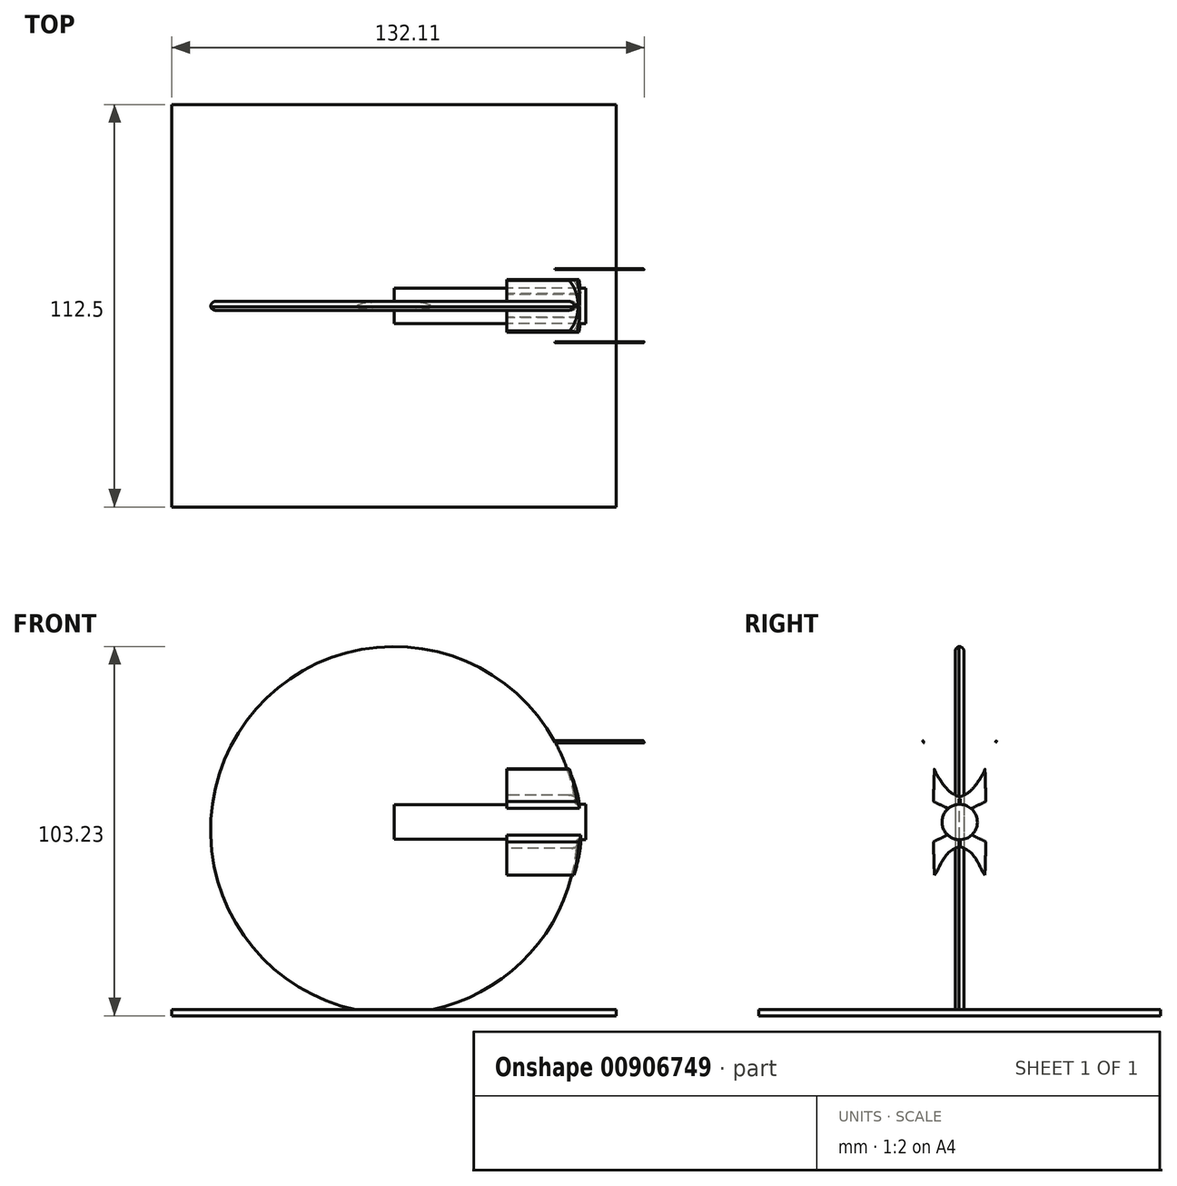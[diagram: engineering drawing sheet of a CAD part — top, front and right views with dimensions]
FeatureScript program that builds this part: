
annotation { "Feature Type Name" : "Feature", "Feature Type Description" : "" }
export const myFeature = defineFeature(function(context is Context, id is Id, definition is map)
    precondition{}
    {
        {
            var Q0;
            Q0=qCreatedBy(makeId("Top.planeOp"),FACE);
            var sketch = newSketch(context, id + "F0", { "sketchPlane" : qUnion([Q0])});
            skArc(sketch, "E0", {"start": v(0, -74.28) * mm, "mid": v(49.1, -56.16) * mm, "end": v(74.07, -10.16) * mm});
            skArc(sketch, "E1", {"start": v(74.12, 9.88) * mm, "mid": v(69.18, -0.13) * mm, "end": v(74.07, -10.16) * mm});
            skArc(sketch, "E2.trimOffspring", {"start": v(74.12, 9.88) * mm, "mid": v(49.23, 56.1) * mm, "end": v(0, 74.35) * mm});
            skLineSegment(sketch, "E3", {"start": v(0, 74.35) * mm, "end": v(0, -74.28) * mm});
            skArc(sketch, "E4", {"start": v(0, -72.43) * mm, "mid": v(75.07, 0.28) * mm, "end": v(0, 72.99) * mm});
            skSolve(sketch);
        }
        {
            var Q0;
            Q0=sQuery(id+"F0.wireOp",EDGE,"E4");
            var Q1;
            Q1=sQuery(id+"F0.wireOp",EDGE,"E3");
            revolve(context, id + "F1", {"bodyType" : ToolBodyType.SURFACE, "surfaceOperationType" : NewSurfaceOperationType.NEW, "surfaceEntities" : qUnion([Q0]), "axis" : qUnion([Q1]), "revolveType" : RevolveType.TWO_DIRECTIONS, "angle" : 10 * degree, "angleBack" : 355 * degree});
        }
        {
            var Q0;
            Q0=sQuery(id+"F0.wireOp",EDGE,"E1");
            var Q1;
            Q1=sQuery(id+"F0.wireOp",EDGE,"E2.trimOffspring");
            var Q2;
            Q2=sQuery(id+"F0.wireOp",EDGE,"E0");
            var Q3;
            Q3=sQuery(id+"F0.wireOp",EDGE,"E3");
            revolve(context, id + "F2", {"bodyType" : ToolBodyType.SURFACE, "surfaceOperationType" : NewSurfaceOperationType.NEW, "surfaceEntities" : qUnion([Q0, Q1, Q2]), "axis" : qUnion([Q3]), "revolveType" : RevolveType.FULL});
        }
        {
            var Q0;
            Q0=qCreatedBy(makeId("Right.planeOp"),FACE);
            cPlane(context, id + "F3", {"entities" : qUnion([Q0]), "cplaneType" : CPlaneType.OFFSET, "offset" : 75 * mm, "width" : 150 * mm, "height" : 150 * mm});
        }
        {
            var Q0;
            Q0=qCreatedBy(id+"F3.planeOp",FACE);
            var sketch = newSketch(context, id + "F4", { "sketchPlane" : qUnion([Q0])});
            skLineSegment(sketch, "E5", {"start": v(0.28, 7.52) * mm, "end": v(0.28, 12.5) * mm});
            skLineSegment(sketch, "E6.MirrorCS", {"start": v(-0.28, 7.52) * mm, "end": v(-0.28, 12.5) * mm});
            skLineSegment(sketch, "E7", {"start": v(0.28, -2.1) * mm, "end": v(0.28, -6.23) * mm});
            skLineSegment(sketch, "E8", {"start": v(-0.28, -2.1) * mm, "end": v(-0.28, -6.23) * mm});
            skCircle(sketch, "E9", {"center": v(0, 3.4) * mm, "radius": 4.14 * mm});
            skLineSegment(sketch, "E10", {"start": v(-0.28, -2.1) * mm, "end": v(-0.28, -0.73) * mm});
            skLineSegment(sketch, "E11", {"start": v(-0.28, -0.73) * mm, "end": v(0.28, -0.73) * mm});
            skLineSegment(sketch, "E12", {"start": v(0.28, -0.73) * mm, "end": v(0.28, -2.1) * mm});
            skPoint(sketch, "E13.orphan", {"position": v(-0.28, 7.2) * mm});
            skPoint(sketch, "E14.orphan", {"position": v(0.28, 7.2) * mm});
            skLineSegment(sketch, "E15", {"start": v(0.28, -6.23) * mm, "end": v(0.28, -6.53) * mm});
            skLineSegment(sketch, "E16", {"start": v(-0.28, -6.23) * mm, "end": v(-0.28, -6.54) * mm});
            skPoint(sketch, "E17.end.orphan", {"position": v(0.28, 13.7) * mm});
            skPoint(sketch, "E17.start.orphan", {"position": v(-0.28, 13.7) * mm});
            skLineSegment(sketch, "E18", {"start": v(-0.28, 12.5) * mm, "end": v(0.28, 12.5) * mm});
            skLineSegment(sketch, "E19", {"start": v(0.28, -6.53) * mm, "end": v(0.28, -6.67) * mm});
            skLineSegment(sketch, "E20", {"start": v(0.28, -6.67) * mm, "end": v(-0.29, -6.67) * mm});
            skLineSegment(sketch, "E21", {"start": v(-0.29, -6.67) * mm, "end": v(-0.28, -6.54) * mm});
            skFitSpline(sketch, "E22", {"points": [v(-0.28, -6.54) * mm, v(-5.63, -10.25) * mm, v(-10.09, -18.03) * mm, v(-10.03, -17.62) * mm], "startDerivative": vector(-11.71, -5.12) * mm, "endDerivative": vector(14.47, 19.81) * mm});
            skFitSpline(sketch, "E23.MirrorCS", {"points": [v(0.28, -6.54) * mm, v(5.63, -10.25) * mm, v(10.09, -18.03) * mm, v(10.03, -17.62) * mm], "startDerivative": vector(11.71, -5.12) * mm, "endDerivative": vector(-14.47, 19.81) * mm});
            skLineSegment(sketch, "E24", {"start": v(10.09, -18.03) * mm, "end": v(10.5, -4.66) * mm});
            skLineSegment(sketch, "E25", {"start": v(10.5, -4.66) * mm, "end": v(1.58, -0.43) * mm});
            skLineSegment(sketch, "E26.MirrorCS", {"start": v(-10.5, -4.66) * mm, "end": v(-1.58, -0.43) * mm});
            skLineSegment(sketch, "E27.MirrorCS", {"start": v(-10.09, -18.03) * mm, "end": v(-10.5, -4.66) * mm});
            skFitSpline(sketch, "E28.MirrorCS", {"points": [v(-0.28, -6.54) * mm, v(-5.63, -10.25) * mm, v(-10.09, -18.03) * mm, v(-10.03, -17.62) * mm], "startDerivative": vector(-11.71, -5.12) * mm, "endDerivative": vector(14.47, 19.81) * mm});
            skLineSegment(sketch, "E29.MirrorCS", {"start": v(-10.1, 24.38) * mm, "end": v(-10.06, 24.14) * mm});
            skFitSpline(sketch, "E30.MirrorCS", {"points": [v(-0.28, 13.33) * mm, v(-5.63, 17.04) * mm, v(-10.1, 24.38) * mm, v(-10.03, 24.41) * mm], "startDerivative": vector(-11.71, 5.12) * mm, "endDerivative": vector(2.1, -0.27) * mm});
            skLineSegment(sketch, "E31.MirrorCS", {"start": v(10.1, 24.38) * mm, "end": v(10.06, 24.14) * mm});
            skFitSpline(sketch, "E32.MirrorCS", {"points": [v(0.28, 13.33) * mm, v(5.63, 17.04) * mm, v(10.1, 24.38) * mm, v(10.03, 24.41) * mm], "startDerivative": vector(11.71, 5.12) * mm, "endDerivative": vector(-2.1, -0.27) * mm});
            skLineSegment(sketch, "E33", {"start": v(-0.28, 13.33) * mm, "end": v(0.28, 13.33) * mm});
            skLineSegment(sketch, "E34", {"start": v(-0.28, -6.23) * mm, "end": v(0.28, -6.23) * mm});
            skFitSpline(sketch, "E35.MirrorCS", {"points": [v(0.28, -6.54) * mm, v(5.63, -10.25) * mm, v(10.09, -18.03) * mm, v(10.03, -17.62) * mm], "startDerivative": vector(11.71, -5.12) * mm, "endDerivative": vector(-14.47, 19.81) * mm});
            skLineSegment(sketch, "E36", {"start": v(0, 3.4) * mm, "end": v(4.14, 3.4) * mm});
            skLineSegment(sketch, "E37", {"start": v(4.14, 3.4) * mm, "end": v(-4.14, 3.4) * mm});
            skLineSegment(sketch, "E38.MirrorCS", {"start": v(-10.5, 11.45) * mm, "end": v(-1.58, 7.22) * mm});
            skLineSegment(sketch, "E39.MirrorCS", {"start": v(-10.09, 24.82) * mm, "end": v(-10.5, 11.45) * mm});
            skFitSpline(sketch, "E40.MirrorCS", {"points": [v(-0.28, 13.33) * mm, v(-5.63, 17.04) * mm, v(-10.09, 24.82) * mm, v(-10.03, 24.41) * mm], "startDerivative": vector(-11.71, 5.12) * mm, "endDerivative": vector(14.47, -19.81) * mm});
            skFitSpline(sketch, "E41.MirrorCS", {"points": [v(0.28, 13.33) * mm, v(5.63, 17.04) * mm, v(10.09, 24.82) * mm, v(10.03, 24.41) * mm], "startDerivative": vector(11.71, 5.12) * mm, "endDerivative": vector(-14.47, -19.81) * mm});
            skLineSegment(sketch, "E42.MirrorCS", {"start": v(10.5, 11.45) * mm, "end": v(1.58, 7.22) * mm});
            skLineSegment(sketch, "E43.MirrorCS", {"start": v(10.09, 24.82) * mm, "end": v(10.5, 11.45) * mm});
            skLineSegment(sketch, "E44", {"start": v(-0.28, -2.1) * mm, "end": v(0.28, -2.1) * mm});
            skLineSegment(sketch, "E45.MirrorCS", {"start": v(-0.28, 8.9) * mm, "end": v(0.28, 8.9) * mm});
            skSolve(sketch);
        }
        {
            var Q0;
            {var subQ0=sQuery(id+"F4.wireOp",EDGE,"E28.MirrorCS");var subQ1=sQuery(id+"F4.wireOp",EDGE,"E27.MirrorCS");var subQ2=makeQuery(id+"F4.imprint","INTERSECT",VERTEX,{"disambiguationData":[OD(0.0)],"derivedFrom":[subQ1,subQ0]});Q0=makeQuery(id+"F4.imprint","IMPRINT",FACE,{"disambiguationData":[TD([[makeQuery(id+"F4.imprint","IMPRINT",EDGE,{"disambiguationData":[TD([[subQ2,-1.0]])],"derivedFrom":subQ1}),1.0]])]});}
            var Q1;
            {var subQ0=sQuery(id+"F4.wireOp",EDGE,"E30.MirrorCS");Q1=makeQuery(id+"F4.imprint","IMPRINT",FACE,{"disambiguationData":[TD([[makeQuery(id+"F4.imprint","IMPRINT",EDGE,{"derivedFrom":subQ0}),1.0]])]});}
            var Q2;
            {var subQ0=sQuery(id+"F4.wireOp",EDGE,"E32.MirrorCS");Q2=makeQuery(id+"F4.imprint","IMPRINT",FACE,{"disambiguationData":[TD([[makeQuery(id+"F4.imprint","IMPRINT",EDGE,{"derivedFrom":subQ0}),-1.0]])]});}
            var Q3;
            {var subQ0=sQuery(id+"F4.wireOp",EDGE,"E35.MirrorCS");var subQ1=sQuery(id+"F4.wireOp",EDGE,"E24");var subQ2=makeQuery(id+"F4.imprint","INTERSECT",VERTEX,{"disambiguationData":[OD(0.0)],"derivedFrom":[subQ1,subQ0]});Q3=makeQuery(id+"F4.imprint","IMPRINT",FACE,{"disambiguationData":[TD([[makeQuery(id+"F4.imprint","IMPRINT",EDGE,{"disambiguationData":[TD([[subQ2,-1.0]])],"derivedFrom":subQ1}),-1.0]])]});}
            var Q4;
            {var subQ0=sQuery(id+"F4.wireOp",EDGE,"E40.MirrorCS");var subQ1=sQuery(id+"F4.wireOp",EDGE,"E39.MirrorCS");var subQ2=makeQuery(id+"F4.imprint","INTERSECT",VERTEX,{"disambiguationData":[OD(0.0)],"derivedFrom":[subQ1,subQ0]});Q4=makeQuery(id+"F4.imprint","IMPRINT",FACE,{"disambiguationData":[TD([[makeQuery(id+"F4.imprint","IMPRINT",EDGE,{"disambiguationData":[TD([[subQ2,-1.0]])],"derivedFrom":subQ1}),-1.0]])]});}
            var Q5;
            {var subQ0=sQuery(id+"F4.wireOp",EDGE,"E40.MirrorCS");var subQ1=sQuery(id+"F4.wireOp",EDGE,"E39.MirrorCS");var subQ2=makeQuery(id+"F4.imprint","INTERSECT",VERTEX,{"disambiguationData":[OD(1.0)],"derivedFrom":[subQ1,subQ0]});Q5=makeQuery(id+"F4.imprint","IMPRINT",FACE,{"disambiguationData":[TD([[makeQuery(id+"F4.imprint","IMPRINT",EDGE,{"disambiguationData":[TD([[subQ2,-1.0]])],"derivedFrom":subQ1}),1.0]])]});}
            var Q6;
            {var subQ0=sQuery(id+"F4.wireOp",EDGE,"E43.MirrorCS");var subQ1=sQuery(id+"F4.wireOp",EDGE,"E41.MirrorCS");var subQ2=makeQuery(id+"F4.imprint","INTERSECT",VERTEX,{"disambiguationData":[OD(0.0)],"derivedFrom":[subQ1,subQ0]});Q6=makeQuery(id+"F4.imprint","IMPRINT",FACE,{"disambiguationData":[TD([[makeQuery(id+"F4.imprint","IMPRINT",EDGE,{"disambiguationData":[TD([[subQ2,-1.0]])],"derivedFrom":subQ1}),-1.0]])]});}
            var Q7;
            {var subQ0=sQuery(id+"F4.wireOp",EDGE,"E32.MirrorCS");var subQ1=sQuery(id+"F4.wireOp",EDGE,"E41.MirrorCS");var subQ2=makeQuery(id+"F4.imprint","INTERSECT",VERTEX,{"derivedFrom":[subQ1,subQ0]});Q7=makeQuery(id+"F4.imprint","IMPRINT",FACE,{"disambiguationData":[TD([[makeQuery(id+"F4.imprint","IMPRINT",EDGE,{"disambiguationData":[TD([[subQ2,1.0]])],"derivedFrom":subQ1}),1.0]])]});}
            var Q8;
            {var subQ0=sQuery(id+"F4.wireOp",EDGE,"E30.MirrorCS");var subQ1=sQuery(id+"F4.wireOp",EDGE,"E29.MirrorCS");var subQ2=makeQuery(id+"F4.imprint","INTERSECT",VERTEX,{"disambiguationData":[OD(0.0)],"derivedFrom":[subQ1,subQ0]});Q8=makeQuery(id+"F4.imprint","IMPRINT",FACE,{"disambiguationData":[TD([[makeQuery(id+"F4.imprint","IMPRINT",EDGE,{"disambiguationData":[TD([[subQ2,-1.0]])],"derivedFrom":subQ1}),1.0]])]});}
            var Q9;
            {var subQ0=sQuery(id+"F4.wireOp",EDGE,"E30.MirrorCS");var subQ1=sQuery(id+"F4.wireOp",EDGE,"E29.MirrorCS");var subQ2=makeQuery(id+"F4.imprint","INTERSECT",VERTEX,{"disambiguationData":[OD(0.0)],"derivedFrom":[subQ1,subQ0]});Q9=makeQuery(id+"F4.imprint","IMPRINT",FACE,{"disambiguationData":[TD([[makeQuery(id+"F4.imprint","IMPRINT",EDGE,{"disambiguationData":[TD([[subQ2,-1.0]])],"derivedFrom":subQ1}),-1.0]])]});}
            var Q10;
            {var subQ0=sQuery(id+"F4.wireOp",EDGE,"E30.MirrorCS");var subQ1=sQuery(id+"F4.wireOp",EDGE,"E29.MirrorCS");var subQ2=makeQuery(id+"F4.imprint","INTERSECT",VERTEX,{"disambiguationData":[OD(1.0)],"derivedFrom":[subQ1,subQ0]});Q10=makeQuery(id+"F4.imprint","IMPRINT",FACE,{"disambiguationData":[TD([[makeQuery(id+"F4.imprint","IMPRINT",EDGE,{"disambiguationData":[TD([[subQ2,1.0]])],"derivedFrom":subQ1}),-1.0]])]});}
            var Q11;
            {var subQ0=sQuery(id+"F4.wireOp",EDGE,"E32.MirrorCS");var subQ1=sQuery(id+"F4.wireOp",EDGE,"E31.MirrorCS");var subQ2=makeQuery(id+"F4.imprint","INTERSECT",VERTEX,{"disambiguationData":[OD(0.0)],"derivedFrom":[subQ1,subQ0]});Q11=makeQuery(id+"F4.imprint","IMPRINT",FACE,{"disambiguationData":[TD([[makeQuery(id+"F4.imprint","IMPRINT",EDGE,{"disambiguationData":[TD([[subQ2,-1.0]])],"derivedFrom":subQ1}),-1.0]])]});}
            var Q12;
            {var subQ0=sQuery(id+"F4.wireOp",EDGE,"E32.MirrorCS");var subQ1=sQuery(id+"F4.wireOp",EDGE,"E31.MirrorCS");var subQ2=makeQuery(id+"F4.imprint","INTERSECT",VERTEX,{"disambiguationData":[OD(0.0)],"derivedFrom":[subQ1,subQ0]});Q12=makeQuery(id+"F4.imprint","IMPRINT",FACE,{"disambiguationData":[TD([[makeQuery(id+"F4.imprint","IMPRINT",EDGE,{"disambiguationData":[TD([[subQ2,-1.0]])],"derivedFrom":subQ1}),1.0]])]});}
            var Q13;
            {var subQ0=sQuery(id+"F4.wireOp",EDGE,"E32.MirrorCS");var subQ1=sQuery(id+"F4.wireOp",EDGE,"E31.MirrorCS");var subQ2=makeQuery(id+"F4.imprint","INTERSECT",VERTEX,{"disambiguationData":[OD(1.0)],"derivedFrom":[subQ1,subQ0]});Q13=makeQuery(id+"F4.imprint","IMPRINT",FACE,{"disambiguationData":[TD([[makeQuery(id+"F4.imprint","IMPRINT",EDGE,{"disambiguationData":[TD([[subQ2,1.0]])],"derivedFrom":subQ1}),1.0]])]});}
            var Q14;
            {var subQ5=sQuery(id+"F4.wireOp",EDGE,"E37");var subQ8=makeQuery(id+"F4.imprint","IMPRINT",VERTEX,{"derivedFrom":subQ5});Q14=makeQuery(id+"F4.imprint","IMPRINT",FACE,{"disambiguationData":[TD([[makeQuery(id+"F4.imprint","IMPRINT",EDGE,{"disambiguationData":[TD([[subQ8,1.0]])],"derivedFrom":subQ5}),-1.0]])]});}
            var Q15;
            {var subQ3=sQuery(id+"F4.wireOp",EDGE,"E15");Q15=makeQuery(id+"F4.imprint","IMPRINT",FACE,{"disambiguationData":[TD([[makeQuery(id+"F4.imprint","IMPRINT",EDGE,{"derivedFrom":subQ3}),-1.0]])]});}
            var Q16;
            Q16=makeQuery(id+"F4.imprint","IMPRINT",FACE,{"disambiguationData":[TD([[makeQuery(id+"F4.imprint","IMPRINT",EDGE,{"derivedFrom":sQuery(id+"F4.wireOp",EDGE,"E7")}),1.0]])]});
            var Q17;
            Q17=makeQuery(id+"F4.imprint","IMPRINT",FACE,{"disambiguationData":[TD([[makeQuery(id+"F4.imprint","IMPRINT",EDGE,{"derivedFrom":sQuery(id+"F4.wireOp",EDGE,"E8")}),-1.0]])]});
            var Q18;
            {var subQ4=sQuery(id+"F4.wireOp",EDGE,"E11");Q18=makeQuery(id+"F4.imprint","IMPRINT",FACE,{"disambiguationData":[TD([[makeQuery(id+"F4.imprint","IMPRINT",EDGE,{"derivedFrom":subQ4}),1.0]])]});}
            var Q19;
            {var subQ15=sQuery(id+"F4.wireOp",EDGE,"E5");Q19=makeQuery(id+"F4.imprint","IMPRINT",FACE,{"disambiguationData":[TD([[makeQuery(id+"F4.imprint","IMPRINT",EDGE,{"derivedFrom":subQ15}),-1.0]])]});}
            extrude(context, id + "F5", {"entities" : qUnion([Q0, Q1, Q2, Q3, Q4, Q5, Q6, Q7, Q8, Q9, Q10, Q11, Q12, Q13, Q14, Q15, Q16, Q17, Q18, Q19]), "depth" : 3 * mm, "offsetDistance" : 25 * mm, "hasSecondDirection" : true, "secondDirectionOppositeDirection" : true, "secondDirectionDepth" : 30 * mm});
        }
        {
            var Q0;
            Q0=qCreatedBy(makeId("Right.planeOp"),FACE);
            var sketch = newSketch(context, id + "F6", { "sketchPlane" : qUnion([Q0])});
            skArc(sketch, "E46.0", {"start": v(1.58, -0.43) * mm, "mid": v(-4.14, 3.4) * mm, "end": v(1.58, 7.22) * mm});
            skArc(sketch, "E47.0", {"start": v(-1.58, 7.22) * mm, "mid": v(4.14, 3.4) * mm, "end": v(-1.58, -0.43) * mm});
            skCircle(sketch, "E48", {"center": v(0, 0) * mm, "radius": 74.8 * mm});
            skCircle(sketch, "E49", {"center": v(0, 3.4) * mm, "radius": 90.06 * mm});
            skLineSegment(sketch, "E50", {"start": v(-74.8, 0) * mm, "end": v(-90, 0) * mm});
            skLineSegment(sketch, "E51", {"start": v(74.8, 0) * mm, "end": v(90, 0) * mm});
            skSolve(sketch);
        }
        {
            var Q0;
            {var subQ0=sQuery(id+"F6.wireOp",EDGE,"E50");Q0=makeQuery(id+"F6.imprint","IMPRINT",FACE,{"disambiguationData":[TD([[makeQuery(id+"F6.imprint","IMPRINT",EDGE,{"derivedFrom":subQ0}),-1.0]])]});}
            var Q1;
            Q1=sQuery(id+"F6.wireOp",EDGE,"E50");
            revolve(context, id + "F7", {"operationType" : NewBodyOperationType.REMOVE, "surfaceOperationType" : NewSurfaceOperationType.NEW, "entities" : qUnion([Q0]), "axis" : qUnion([Q1]), "revolveType" : RevolveType.FULL, "oppositeDirection" : true});
        }
        {
            var Q0;
            Q0=makeQuery(id+"F2.opRevolve","SWEPT_BODY",BODY,{"disambiguationData":[OSD([sQuery(id+"F0.wireOp",EDGE,"E2.trimOffspring")])]});
            var Q1;
            Q1=makeQuery(id+"F1.opRevolve","SWEPT_BODY",BODY,{"disambiguationData":[OSD([sQuery(id+"F0.wireOp",EDGE,"E4")])]});
            var Q2;
            Q2=makeQuery(id+"F5.opExtrude","SWEPT_BODY",BODY,{"disambiguationData":[OSD([sQuery(id+"F4.wireOp",EDGE,"E5"),sQuery(id+"F4.wireOp",EDGE,"E6.MirrorCS"),sQuery(id+"F4.wireOp",EDGE,"E7"),sQuery(id+"F4.wireOp",EDGE,"E8"),sQuery(id+"F4.wireOp",EDGE,"E9"),sQuery(id+"F4.wireOp",EDGE,"E10"),sQuery(id+"F4.wireOp",EDGE,"E11"),sQuery(id+"F4.wireOp",EDGE,"E12"),sQuery(id+"F4.wireOp",EDGE,"E18"),sQuery(id+"F4.wireOp",EDGE,"E19"),sQuery(id+"F4.wireOp",EDGE,"E20"),sQuery(id+"F4.wireOp",EDGE,"E21"),sQuery(id+"F4.wireOp",EDGE,"E25"),sQuery(id+"F4.wireOp",EDGE,"E26.MirrorCS"),sQuery(id+"F4.wireOp",EDGE,"E27.MirrorCS"),sQuery(id+"F4.wireOp",EDGE,"E28.MirrorCS"),sQuery(id+"F4.wireOp",EDGE,"E30.MirrorCS"),sQuery(id+"F4.wireOp",EDGE,"E32.MirrorCS"),sQuery(id+"F4.wireOp",EDGE,"E33"),sQuery(id+"F4.wireOp",EDGE,"E34"),sQuery(id+"F4.wireOp",EDGE,"E24"),sQuery(id+"F4.wireOp",EDGE,"E35.MirrorCS"),sQuery(id+"F4.wireOp",EDGE,"E38.MirrorCS"),sQuery(id+"F4.wireOp",EDGE,"E39.MirrorCS"),sQuery(id+"F4.wireOp",EDGE,"E40.MirrorCS"),sQuery(id+"F4.wireOp",EDGE,"E41.MirrorCS"),sQuery(id+"F4.wireOp",EDGE,"E42.MirrorCS"),sQuery(id+"F4.wireOp",EDGE,"E43.MirrorCS"),sQuery(id+"F4.wireOp",EDGE,"E32.MirrorCS"),sQuery(id+"F4.wireOp",EDGE,"E30.MirrorCS")])]});
            var Q3;
            Q3=makeQuery(id+"FB0Hu42CFCcYgfv_2.opExtrude","SWEPT_BODY",BODY,{"disambiguationData":[OSD([sQuery(id+"F4.wireOp",EDGE,"E9")])]});
            var Q4;
            Q4=qCreatedBy(makeId("Origin.pointOp"),VERTEX);
            transform(context, id + "F8", {"entities" : qUnion([Q0, Q1, Q2, Q3]), "transformType" : TransformType.SCALE_UNIFORMLY, "scale" : .7, "scalePoint" : qUnion([Q4]), "makeCopy" : false});
        }
        {
            var Q0;
            Q0=qCreatedBy(makeId("Right.planeOp"),FACE);
            var sketch = newSketch(context, id + "F9", { "sketchPlane" : qUnion([Q0])});
            skCircle(sketch, "E52", {"center": v(0, 2.26) * mm, "radius": 4.95 * mm});
            skSolve(sketch);
        }
        {
            var Q0;
            Q0 = qSketchRegion(id + "F9", true);
            var Q1;
            {var subQ15=sQuery(id+"F4.wireOp",EDGE,"E5");Q1=makeQuery(id+"F4.imprint","IMPRINT",FACE,{"disambiguationData":[TD([[makeQuery(id+"F4.imprint","IMPRINT",EDGE,{"derivedFrom":subQ15}),-1.0]])]});}
            extrude(context, id + "F10", {"entities" : qUnion([Q0, Q1]), "operationType" : NewBodyOperationType.ADD, "depth" : 53.7 * mm, "offsetDistance" : 25 * mm});
        }
        {
            var Q0;
            Q0=makeQuery(id+"F10.opExtrude","SWEPT_BODY",BODY,{"disambiguationData":[OSD([sQuery(id+"F4.wireOp",EDGE,"E5"),sQuery(id+"F4.wireOp",EDGE,"E6.MirrorCS"),sQuery(id+"F4.wireOp",EDGE,"E9"),sQuery(id+"F4.wireOp",EDGE,"E18"),sQuery(id+"F4.wireOp",EDGE,"E29.MirrorCS"),sQuery(id+"F4.wireOp",EDGE,"E31.MirrorCS"),sQuery(id+"F4.wireOp",EDGE,"E33"),sQuery(id+"F4.wireOp",EDGE,"E38.MirrorCS"),sQuery(id+"F4.wireOp",EDGE,"E39.MirrorCS"),sQuery(id+"F4.wireOp",EDGE,"E40.MirrorCS"),sQuery(id+"F4.wireOp",EDGE,"E41.MirrorCS"),sQuery(id+"F4.wireOp",EDGE,"E42.MirrorCS"),sQuery(id+"F4.wireOp",EDGE,"E43.MirrorCS"),sQuery(id+"F4.wireOp",EDGE,"E32.MirrorCS"),sQuery(id+"F4.wireOp",EDGE,"E30.MirrorCS")])]});
            deleteBodies(context, id + "F11", {"entities" : qUnion([Q0])});
        }
        {
            var Q0;
            Q0=qCreatedBy(makeId("Front.planeOp"),FACE);
            var sketch = newSketch(context, id + "F12", { "sketchPlane" : qUnion([Q0])});
            skCircle(sketch, "E53", {"center": v(0, 0) * mm, "radius": 51.33 * mm});
            skSolve(sketch);
        }
        {
            var Q0;
            Q0 = qSketchRegion(id + "F12", true);
            extrude(context, id + "F13", {"entities" : qUnion([Q0]), "operationType" : NewBodyOperationType.ADD, "oppositeDirection" : true, "depth" : 2.5 * mm, "offsetDistance" : 25 * mm, "symmetric" : true});
        }
        {
            var Q0;
            Q0=makeQuery(id+"F13.opExtrude","CAP_EDGE",EDGE,{"disambiguationData":[OSD([sQuery(id+"F12.wireOp",EDGE,"E53")])],"isStart":false});
            fillet(context, id + "F14", {"entities" : qUnion([Q0]), "radius" : 1.5 * mm, "tangentPropagation" : true, "allowEdgeOverflow" : false});
        }
        {
            var Q0;
            {var subQ0=sQuery(id+"F12.wireOp",EDGE,"E53");Q0=makeQuery(id+"F13.boolean.opBoolean","SPLIT",EDGE,{"disambiguationData":[TD([makeQuery(id+"F5.opExtrude","SWEPT_FACE",FACE,{"disambiguationData":[OSD([sQuery(id+"F4.wireOp",EDGE,"E20")])]})])],"derivedFrom":makeQuery(id+"F13.opExtrude","CAP_EDGE",EDGE,{"disambiguationData":[OSD([subQ0])],"isStart":true})});}
            fillet(context, id + "F15", {"entities" : qUnion([Q0]), "radius" : 1.5 * mm, "tangentPropagation" : true, "allowEdgeOverflow" : false});
        }
        {
            var Q0;
            Q0=qCreatedBy(makeId("Top.planeOp"),FACE);
            cPlane(context, id + "F16", {"entities" : qUnion([Q0]), "cplaneType" : CPlaneType.OFFSET, "offset" : 51.9 * mm, "oppositeDirection" : true, "width" : 150 * mm, "height" : 150 * mm});
        }
        {
            var Q0;
            Q0=qCreatedBy(id+"F16.planeOp",FACE);
            var sketch = newSketch(context, id + "F17", { "sketchPlane" : qUnion([Q0])});
            skLineSegment(sketch, "E54.bottom", {"start": v(62.13, -56.25) * mm, "end": v(-62.13, -56.25) * mm});
            skLineSegment(sketch, "E54.top", {"start": v(62.13, 56.25) * mm, "end": v(-62.13, 56.25) * mm});
            skLineSegment(sketch, "E54.left", {"start": v(62.13, -56.25) * mm, "end": v(62.13, 56.25) * mm});
            skLineSegment(sketch, "E54.right", {"start": v(-62.13, -56.25) * mm, "end": v(-62.13, 56.25) * mm});
            skPoint(sketch, "E54.middle", {"position": v(0, 0) * mm});
            skSolve(sketch);
        }
        {
            var Q0;
            Q0=makeQuery(id+"F17.imprint","IMPRINT",FACE,{"disambiguationData":[TD([[makeQuery(id+"F17.imprint","IMPRINT",EDGE,{"derivedFrom":sQuery(id+"F17.wireOp",EDGE,"E54.bottom")}),-1.0]])]});
            extrude(context, id + "F18", {"entities" : qUnion([Q0]), "operationType" : NewBodyOperationType.ADD, "depth" : 1.7 * mm, "offsetDistance" : 25 * mm});
        }
    });
